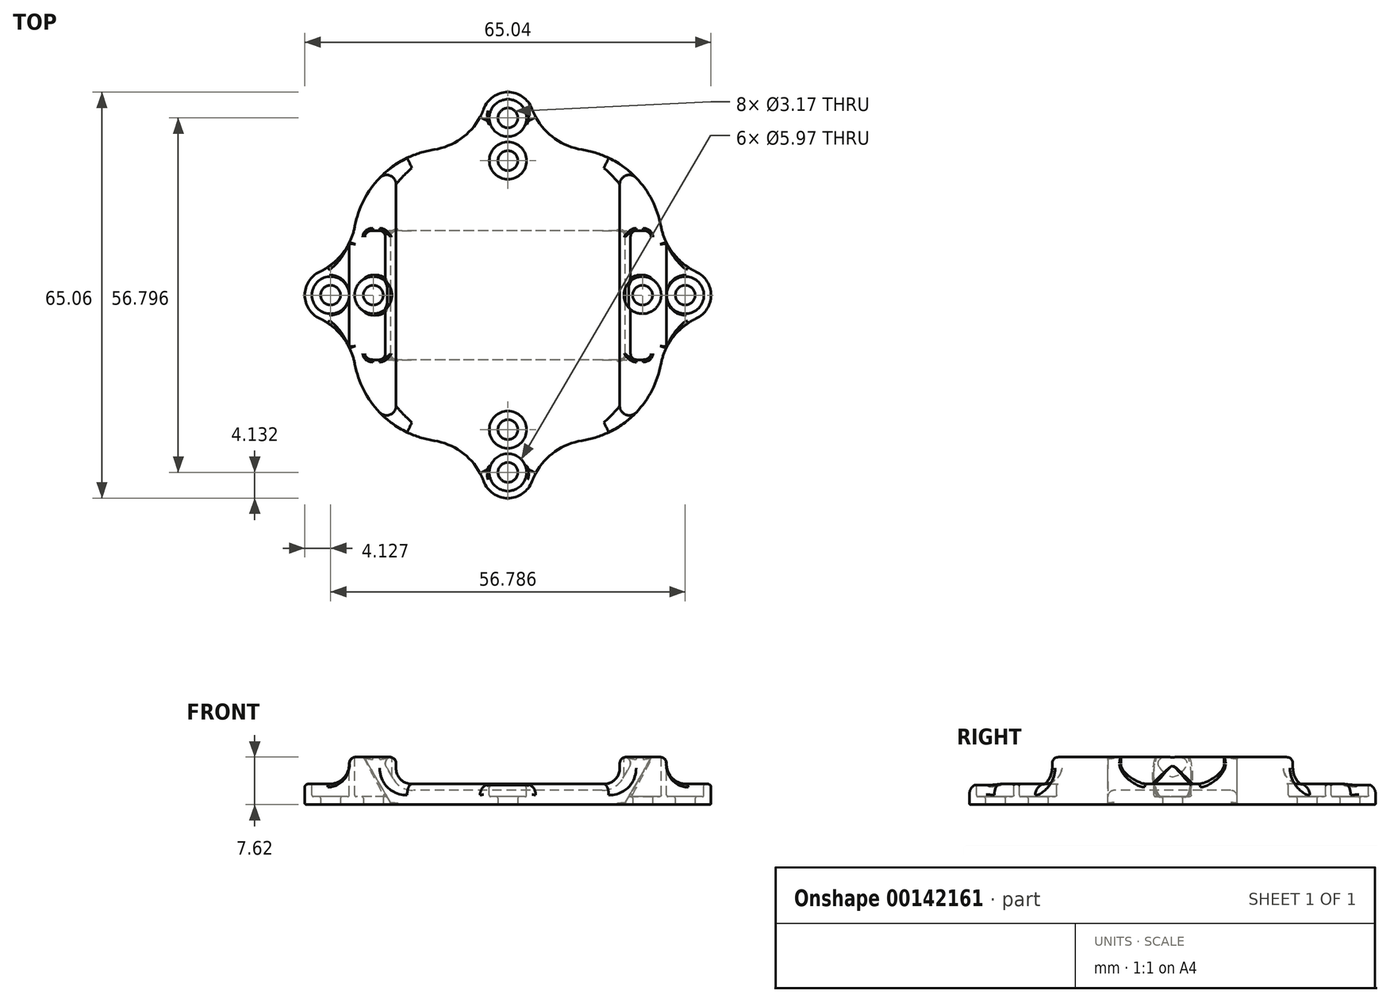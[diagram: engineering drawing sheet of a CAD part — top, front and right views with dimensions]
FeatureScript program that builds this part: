
annotation { "Feature Type Name" : "Feature", "Feature Type Description" : "" }
export const myFeature = defineFeature(function(context is Context, id is Id, definition is map)
    precondition{}
    {
        {
            var Q0;
            Q0=qCreatedBy(makeId("Top.planeOp"),FACE);
            var sketch = newSketch(context, id + "F0", { "sketchPlane" : qUnion([Q0])});
            skLineSegment(sketch, "E0", {"start": v(-21.55, 0) * mm, "end": v(0, 21.55) * mm});
            skLineSegment(sketch, "E1", {"start": v(0, 21.55) * mm, "end": v(21.55, 0) * mm});
            skLineSegment(sketch, "E2", {"start": v(21.55, 0) * mm, "end": v(0, -21.55) * mm});
            skLineSegment(sketch, "E3", {"start": v(0, -21.55) * mm, "end": v(-21.55, 0) * mm});
            skCircle(sketch, "E4", {"center": v(0, 21.55) * mm, "radius": 1.59 * mm});
            skCircle(sketch, "E5", {"center": v(-21.55, 0) * mm, "radius": 1.59 * mm});
            skCircle(sketch, "E6", {"center": v(0, -21.55) * mm, "radius": 1.59 * mm});
            skCircle(sketch, "E7", {"center": v(21.55, 0) * mm, "radius": 1.59 * mm});
            skCircle(sketch, "E8", {"center": v(0, 28.4) * mm, "radius": 1.59 * mm});
            skCircle(sketch, "E9", {"center": v(0, -28.4) * mm, "radius": 1.59 * mm});
            skCircle(sketch, "E10", {"center": v(28.4, 0) * mm, "radius": 1.59 * mm});
            skCircle(sketch, "E11", {"center": v(-28.4, 0) * mm, "radius": 1.59 * mm});
            skLineSegment(sketch, "E12.bottom", {"start": v(9.53, 23.5) * mm, "end": v(-9.53, 23.5) * mm});
            skLineSegment(sketch, "E12.top", {"start": v(9.53, -23.5) * mm, "end": v(-9.53, -23.5) * mm});
            skLineSegment(sketch, "E12.left", {"start": v(24.77, 8.26) * mm, "end": v(24.77, -8.26) * mm});
            skLineSegment(sketch, "E12.right", {"start": v(-24.77, 8.26) * mm, "end": v(-24.77, -8.26) * mm});
            skPoint(sketch, "E12.middle", {"position": v(0, 0) * mm});
            skLineSegment(sketch, "E13.bottom", {"start": v(0, 32.53) * mm, "end": v(0, 32.53) * mm});
            skLineSegment(sketch, "E13.top", {"start": v(4.13, 10.58) * mm, "end": v(-4.13, 10.58) * mm});
            skLineSegment(sketch, "E13.left", {"start": v(4.13, 28.4) * mm, "end": v(4.13, 10.58) * mm});
            skLineSegment(sketch, "E13.right", {"start": v(-4.13, 28.4) * mm, "end": v(-4.13, 10.58) * mm});
            skLineSegment(sketch, "E14.bottom", {"start": v(28.4, 4.13) * mm, "end": v(10.58, 4.13) * mm});
            skLineSegment(sketch, "E14.top", {"start": v(28.4, -4.13) * mm, "end": v(10.58, -4.13) * mm});
            skLineSegment(sketch, "E14.left", {"start": v(32.52, 0) * mm, "end": v(32.52, 0) * mm});
            skLineSegment(sketch, "E14.right", {"start": v(10.58, 4.13) * mm, "end": v(10.58, -4.13) * mm});
            skLineSegment(sketch, "E15.bottom", {"start": v(4.13, -10.58) * mm, "end": v(-4.13, -10.58) * mm});
            skLineSegment(sketch, "E15.top", {"start": v(0, -32.53) * mm, "end": v(0, -32.53) * mm});
            skLineSegment(sketch, "E15.left", {"start": v(4.13, -10.58) * mm, "end": v(4.13, -28.4) * mm});
            skLineSegment(sketch, "E15.right", {"start": v(-4.13, -10.58) * mm, "end": v(-4.13, -28.4) * mm});
            skLineSegment(sketch, "E16.bottom", {"start": v(-10.58, 4.13) * mm, "end": v(-28.4, 4.13) * mm});
            skLineSegment(sketch, "E16.top", {"start": v(-10.58, -4.13) * mm, "end": v(-28.4, -4.13) * mm});
            skLineSegment(sketch, "E16.left", {"start": v(-10.58, 4.13) * mm, "end": v(-10.58, -4.13) * mm});
            skLineSegment(sketch, "E16.right", {"start": v(-32.52, 0) * mm, "end": v(-32.52, 0) * mm});
            skPoint(sketch, "E17.visualSharp", {"position": v(-32.52, 4.13) * mm});
            skArc(sketch, "E17.filletArc", {"start": v(-28.4, 4.13) * mm, "mid": v(-31.31, 2.92) * mm, "end": v(-32.52, 0) * mm});
            skPoint(sketch, "E18.visualSharp", {"position": v(-32.52, -4.13) * mm});
            skArc(sketch, "E18.filletArc", {"start": v(-32.52, 0) * mm, "mid": v(-31.31, -2.92) * mm, "end": v(-28.4, -4.13) * mm});
            skPoint(sketch, "E19.visualSharp", {"position": v(32.52, 4.13) * mm});
            skArc(sketch, "E19.filletArc", {"start": v(32.52, 0) * mm, "mid": v(31.31, 2.92) * mm, "end": v(28.4, 4.13) * mm});
            skPoint(sketch, "E20.visualSharp", {"position": v(32.52, -4.13) * mm});
            skArc(sketch, "E20.filletArc", {"start": v(28.4, -4.13) * mm, "mid": v(31.31, -2.92) * mm, "end": v(32.52, 0) * mm});
            skPoint(sketch, "E21.visualSharp", {"position": v(4.13, -32.53) * mm});
            skArc(sketch, "E21.filletArc", {"start": v(0, -32.53) * mm, "mid": v(2.92, -31.32) * mm, "end": v(4.13, -28.4) * mm});
            skPoint(sketch, "E22.visualSharp", {"position": v(-4.13, -32.53) * mm});
            skArc(sketch, "E22.filletArc", {"start": v(-4.13, -28.4) * mm, "mid": v(-2.92, -31.32) * mm, "end": v(0, -32.53) * mm});
            skPoint(sketch, "E23.visualSharp", {"position": v(-4.13, 32.53) * mm});
            skArc(sketch, "E23.filletArc", {"start": v(0, 32.53) * mm, "mid": v(-2.92, 31.32) * mm, "end": v(-4.13, 28.4) * mm});
            skPoint(sketch, "E24.visualSharp", {"position": v(4.13, 32.53) * mm});
            skArc(sketch, "E24.filletArc", {"start": v(4.13, 28.4) * mm, "mid": v(2.92, 31.32) * mm, "end": v(0, 32.53) * mm});
            skPoint(sketch, "E25.visualSharp", {"position": v(-24.77, 23.5) * mm});
            skArc(sketch, "E25.filletArc", {"start": v(-9.53, 23.5) * mm, "mid": v(-20.3, 19.03) * mm, "end": v(-24.77, 8.26) * mm});
            skPoint(sketch, "E26.visualSharp", {"position": v(24.77, 23.5) * mm});
            skArc(sketch, "E26.filletArc", {"start": v(24.77, 8.26) * mm, "mid": v(20.3, 19.03) * mm, "end": v(9.53, 23.5) * mm});
            skPoint(sketch, "E27.visualSharp", {"position": v(24.77, -23.5) * mm});
            skArc(sketch, "E27.filletArc", {"start": v(9.53, -23.5) * mm, "mid": v(20.3, -19.03) * mm, "end": v(24.77, -8.26) * mm});
            skPoint(sketch, "E28.visualSharp", {"position": v(-24.77, -23.5) * mm});
            skArc(sketch, "E28.filletArc", {"start": v(-24.77, -8.26) * mm, "mid": v(-20.3, -19.03) * mm, "end": v(-9.53, -23.5) * mm});
            skSolve(sketch);
        }
        {
            var Q0;
            Q0=makeQuery(id+"F0.imprint","IMPRINT",FACE,{"disambiguationData":[TD([[makeQuery(id+"F0.imprint","IMPRINT",EDGE,{"derivedFrom":sQuery(id+"F0.wireOp",EDGE,"E8")}),-1.0]])]});
            var Q1;
            Q1=makeQuery(id+"F0.imprint","IMPRINT",FACE,{"disambiguationData":[TD([[makeQuery(id+"F0.imprint","IMPRINT",EDGE,{"derivedFrom":sQuery(id+"F0.wireOp",EDGE,"E9")}),-1.0]])]});
            var Q2;
            Q2=makeQuery(id+"F0.imprint","IMPRINT",FACE,{"disambiguationData":[TD([[makeQuery(id+"F0.imprint","IMPRINT",EDGE,{"derivedFrom":sQuery(id+"F0.wireOp",EDGE,"E10")}),-1.0]])]});
            var Q3;
            Q3=makeQuery(id+"F0.imprint","IMPRINT",FACE,{"disambiguationData":[TD([[makeQuery(id+"F0.imprint","IMPRINT",EDGE,{"derivedFrom":sQuery(id+"F0.wireOp",EDGE,"E11")}),-1.0]])]});
            var Q4;
            {var subQ0=sQuery(id+"F0.wireOp",EDGE,"E25.filletArc");Q4=makeQuery(id+"F0.imprint","IMPRINT",FACE,{"disambiguationData":[TD([[makeQuery(id+"F0.imprint","IMPRINT",EDGE,{"derivedFrom":subQ0}),1.0]])]});}
            var Q5;
            {var subQ5=sQuery(id+"F0.wireOp",EDGE,"E26.filletArc");Q5=makeQuery(id+"F0.imprint","IMPRINT",FACE,{"disambiguationData":[TD([[makeQuery(id+"F0.imprint","IMPRINT",EDGE,{"derivedFrom":subQ5}),1.0]])]});}
            var Q6;
            {var subQ5=sQuery(id+"F0.wireOp",EDGE,"E27.filletArc");Q6=makeQuery(id+"F0.imprint","IMPRINT",FACE,{"disambiguationData":[TD([[makeQuery(id+"F0.imprint","IMPRINT",EDGE,{"derivedFrom":subQ5}),1.0]])]});}
            var Q7;
            {var subQ5=sQuery(id+"F0.wireOp",EDGE,"E28.filletArc");Q7=makeQuery(id+"F0.imprint","IMPRINT",FACE,{"disambiguationData":[TD([[makeQuery(id+"F0.imprint","IMPRINT",EDGE,{"derivedFrom":subQ5}),1.0]])]});}
            var Q8;
            {var subQ5=sQuery(id+"F0.wireOp",EDGE,"E0");var subQ7=sQuery(id+"F0.wireOp",EDGE,"E5");var subQ8=makeQuery(id+"F0.imprint","INTERSECT",VERTEX,{"derivedFrom":[subQ5,subQ7]});Q8=makeQuery(id+"F0.imprint","IMPRINT",FACE,{"disambiguationData":[TD([[makeQuery(id+"F0.imprint","IMPRINT",EDGE,{"disambiguationData":[TD([[subQ8,-1.0]])],"derivedFrom":subQ5}),1.0]])]});}
            var Q9;
            {var subQ1=sQuery(id+"F0.wireOp",EDGE,"E0");var subQ9=sQuery(id+"F0.wireOp",EDGE,"E13.right");var subQ11=makeQuery(id+"F0.imprint","INTERSECT",VERTEX,{"derivedFrom":[subQ1,subQ9]});Q9=makeQuery(id+"F0.imprint","IMPRINT",FACE,{"disambiguationData":[TD([[makeQuery(id+"F0.imprint","IMPRINT",EDGE,{"disambiguationData":[TD([[subQ11,-1.0]])],"derivedFrom":subQ1}),1.0]])]});}
            var Q10;
            {var subQ0=sQuery(id+"F0.wireOp",EDGE,"E14.bottom");var subQ6=sQuery(id+"F0.wireOp",EDGE,"E1");var subQ11=makeQuery(id+"F0.imprint","INTERSECT",VERTEX,{"derivedFrom":[subQ6,subQ0]});Q10=makeQuery(id+"F0.imprint","IMPRINT",FACE,{"disambiguationData":[TD([[makeQuery(id+"F0.imprint","IMPRINT",EDGE,{"disambiguationData":[TD([[subQ11,-1.0]])],"derivedFrom":subQ6}),1.0]])]});}
            var Q11;
            {var subQ0=sQuery(id+"F0.wireOp",EDGE,"E15.left");var subQ9=sQuery(id+"F0.wireOp",EDGE,"E2");var subQ11=makeQuery(id+"F0.imprint","INTERSECT",VERTEX,{"derivedFrom":[subQ9,subQ0]});Q11=makeQuery(id+"F0.imprint","IMPRINT",FACE,{"disambiguationData":[TD([[makeQuery(id+"F0.imprint","IMPRINT",EDGE,{"disambiguationData":[TD([[subQ11,-1.0]])],"derivedFrom":subQ9}),1.0]])]});}
            var Q12;
            {var subQ10=sQuery(id+"F0.wireOp",EDGE,"E13.top");Q12=makeQuery(id+"F0.imprint","IMPRINT",FACE,{"disambiguationData":[TD([[makeQuery(id+"F0.imprint","IMPRINT",EDGE,{"derivedFrom":subQ10}),1.0]])]});}
            var Q13;
            {var subQ0=sQuery(id+"F0.wireOp",EDGE,"E13.top");Q13=makeQuery(id+"F0.imprint","IMPRINT",FACE,{"disambiguationData":[TD([[makeQuery(id+"F0.imprint","IMPRINT",EDGE,{"derivedFrom":subQ0}),-1.0]])]});}
            var Q14;
            {var subQ0=sQuery(id+"F0.wireOp",EDGE,"E16.left");Q14=makeQuery(id+"F0.imprint","IMPRINT",FACE,{"disambiguationData":[TD([[makeQuery(id+"F0.imprint","IMPRINT",EDGE,{"derivedFrom":subQ0}),-1.0]])]});}
            var Q15;
            {var subQ8=sQuery(id+"F0.wireOp",EDGE,"E15.bottom");Q15=makeQuery(id+"F0.imprint","IMPRINT",FACE,{"disambiguationData":[TD([[makeQuery(id+"F0.imprint","IMPRINT",EDGE,{"derivedFrom":subQ8}),1.0]])]});}
            var Q16;
            {var subQ0=sQuery(id+"F0.wireOp",EDGE,"E14.right");Q16=makeQuery(id+"F0.imprint","IMPRINT",FACE,{"disambiguationData":[TD([[makeQuery(id+"F0.imprint","IMPRINT",EDGE,{"derivedFrom":subQ0}),1.0]])]});}
            var Q17;
            {var subQ0=sQuery(id+"F0.wireOp",EDGE,"E16.left");Q17=makeQuery(id+"F0.imprint","IMPRINT",FACE,{"disambiguationData":[TD([[makeQuery(id+"F0.imprint","IMPRINT",EDGE,{"derivedFrom":subQ0}),-1.0]])]});}
            extrude(context, id + "F1", {"entities" : qUnion([Q0, Q1, Q2, Q3, Q4, Q5, Q6, Q7, Q8, Q9, Q10, Q11, Q12, Q13, Q14, Q15, Q16, Q17]), "depth" : 7.62 * mm});
        }
        {
            var Q0;
            Q0=makeQuery(id+"F1.opExtrude","SWEPT_EDGE",EDGE,{"disambiguationData":[OSD([sQuery(id+"F0.wireOp",EDGE,"E12.bottom"),sQuery(id+"F0.wireOp",EDGE,"E13.left")])]});
            var Q1;
            Q1=makeQuery(id+"F1.opExtrude","SWEPT_EDGE",EDGE,{"disambiguationData":[OSD([sQuery(id+"F0.wireOp",EDGE,"E12.bottom"),sQuery(id+"F0.wireOp",EDGE,"E13.right")])]});
            var Q2;
            Q2=makeQuery(id+"F1.opExtrude","SWEPT_EDGE",EDGE,{"disambiguationData":[OSD([sQuery(id+"F0.wireOp",EDGE,"E12.top"),sQuery(id+"F0.wireOp",EDGE,"E15.right")])]});
            var Q3;
            Q3=makeQuery(id+"F1.opExtrude","SWEPT_EDGE",EDGE,{"disambiguationData":[OSD([sQuery(id+"F0.wireOp",EDGE,"E12.top"),sQuery(id+"F0.wireOp",EDGE,"E15.left")])]});
            fillet(context, id + "F2", {"entities" : qUnion([Q0, Q1, Q2, Q3]), "radius" : 10.16 * mm, "tangentPropagation" : true, "allowEdgeOverflow" : false});
        }
        {
            var Q0;
            Q0=makeQuery(id+"F1.opExtrude","CAP_FACE",FACE,{"disambiguationData":[OSD([sQuery(id+"F0.wireOp",EDGE,"E4"),sQuery(id+"F0.wireOp",EDGE,"E5"),sQuery(id+"F0.wireOp",EDGE,"E6"),sQuery(id+"F0.wireOp",EDGE,"E7"),sQuery(id+"F0.wireOp",EDGE,"E8"),sQuery(id+"F0.wireOp",EDGE,"E9"),sQuery(id+"F0.wireOp",EDGE,"E10"),sQuery(id+"F0.wireOp",EDGE,"E11"),sQuery(id+"F0.wireOp",EDGE,"E12.bottom"),sQuery(id+"F0.wireOp",EDGE,"E12.top"),sQuery(id+"F0.wireOp",EDGE,"E12.left"),sQuery(id+"F0.wireOp",EDGE,"E12.right"),sQuery(id+"F0.wireOp",EDGE,"E13.left"),sQuery(id+"F0.wireOp",EDGE,"E13.right"),sQuery(id+"F0.wireOp",EDGE,"E14.bottom"),sQuery(id+"F0.wireOp",EDGE,"E14.top"),sQuery(id+"F0.wireOp",EDGE,"E15.left"),sQuery(id+"F0.wireOp",EDGE,"E15.right"),sQuery(id+"F0.wireOp",EDGE,"E16.bottom"),sQuery(id+"F0.wireOp",EDGE,"E16.top"),sQuery(id+"F0.wireOp",EDGE,"E17.filletArc"),sQuery(id+"F0.wireOp",EDGE,"E18.filletArc"),sQuery(id+"F0.wireOp",EDGE,"E19.filletArc"),sQuery(id+"F0.wireOp",EDGE,"E20.filletArc"),sQuery(id+"F0.wireOp",EDGE,"E21.filletArc"),sQuery(id+"F0.wireOp",EDGE,"E22.filletArc"),sQuery(id+"F0.wireOp",EDGE,"E23.filletArc"),sQuery(id+"F0.wireOp",EDGE,"E24.filletArc"),sQuery(id+"F0.wireOp",EDGE,"E25.filletArc"),sQuery(id+"F0.wireOp",EDGE,"E26.filletArc"),sQuery(id+"F0.wireOp",EDGE,"E27.filletArc"),sQuery(id+"F0.wireOp",EDGE,"E28.filletArc")])],"isStart":false});
            var sketch = newSketch(context, id + "F3", { "sketchPlane" : qUnion([Q0])});
            skCircle(sketch, "E29", {"center": v(0, 28.4) * mm, "radius": 2.98 * mm});
            skCircle(sketch, "E30", {"center": v(0, 21.55) * mm, "radius": 2.98 * mm});
            skCircle(sketch, "E31", {"center": v(0, -21.55) * mm, "radius": 2.98 * mm});
            skCircle(sketch, "E32", {"center": v(0, -28.4) * mm, "radius": 2.98 * mm});
            skCircle(sketch, "E33", {"center": v(-21.55, 0) * mm, "radius": 2.98 * mm});
            skCircle(sketch, "E34", {"center": v(21.55, 0) * mm, "radius": 2.98 * mm});
            skCircle(sketch, "E35", {"center": v(28.4, 0) * mm, "radius": 2.98 * mm});
            skCircle(sketch, "E36", {"center": v(-28.4, 0) * mm, "radius": 2.98 * mm});
            skSolve(sketch);
        }
        {
            var Q0;
            Q0 = qSketchRegion(id + "F3", true);
            extrude(context, id + "F4", {"entities" : qUnion([Q0]), "operationType" : NewBodyOperationType.REMOVE, "oppositeDirection" : true, "depth" : 6.35 * mm});
        }
        {
            var Q0;
            Q0=qCreatedBy(makeId("Front.planeOp"),FACE);
            var sketch = newSketch(context, id + "F5", { "sketchPlane" : qUnion([Q0])});
            skLineSegment(sketch, "E37.bottom", {"start": v(17.9, 3.3) * mm, "end": v(-17.9, 3.3) * mm});
            skLineSegment(sketch, "E37.top", {"start": v(17.9, 28.7) * mm, "end": v(-17.9, 28.7) * mm});
            skLineSegment(sketch, "E37.left", {"start": v(17.9, 3.3) * mm, "end": v(17.9, 28.7) * mm});
            skLineSegment(sketch, "E37.right", {"start": v(-17.9, 3.3) * mm, "end": v(-17.9, 28.7) * mm});
            skPoint(sketch, "E37.middle", {"position": v(0, 16) * mm});
            skPoint(sketch, "E38.visualSharp", {"position": v(-17.9, 3.3) * mm});
            skLineSegment(sketch, "E38.filletArc", {"start": v(-17.9, 3.3) * mm, "end": v(-17.9, 3.3) * mm});
            skPoint(sketch, "E39.visualSharp", {"position": v(17.9, 3.3) * mm});
            skLineSegment(sketch, "E39.filletArc", {"start": v(17.9, 3.3) * mm, "end": v(17.9, 3.3) * mm});
            skLineSegment(sketch, "E40.bottom", {"start": v(28.58, 3.3) * mm, "end": v(38.1, 3.3) * mm});
            skLineSegment(sketch, "E40.top", {"start": v(25.4, 28.7) * mm, "end": v(38.1, 28.7) * mm});
            skLineSegment(sketch, "E40.left", {"start": v(25.4, 6.48) * mm, "end": v(25.4, 28.7) * mm});
            skLineSegment(sketch, "E40.right", {"start": v(38.1, 3.3) * mm, "end": v(38.1, 28.7) * mm});
            skLineSegment(sketch, "E41.bottom", {"start": v(-28.58, 3.3) * mm, "end": v(-38.1, 3.3) * mm});
            skLineSegment(sketch, "E41.top", {"start": v(-25.4, 28.7) * mm, "end": v(-38.1, 28.7) * mm});
            skLineSegment(sketch, "E41.left", {"start": v(-25.4, 6.48) * mm, "end": v(-25.4, 28.7) * mm});
            skLineSegment(sketch, "E41.right", {"start": v(-38.1, 3.3) * mm, "end": v(-38.1, 28.7) * mm});
            skPoint(sketch, "E42.visualSharp", {"position": v(-25.4, 3.3) * mm});
            skArc(sketch, "E42.filletArc", {"start": v(-28.58, 3.3) * mm, "mid": v(-26.33, 4.23) * mm, "end": v(-25.4, 6.48) * mm});
            skPoint(sketch, "E43.visualSharp", {"position": v(25.4, 3.3) * mm});
            skArc(sketch, "E43.filletArc", {"start": v(25.4, 6.48) * mm, "mid": v(26.33, 4.23) * mm, "end": v(28.58, 3.3) * mm});
            skSolve(sketch);
        }
        {
            var Q0;
            Q0 = qSketchRegion(id + "F5", true);
            extrude(context, id + "F6", {"entities" : qUnion([Q0]), "operationType" : NewBodyOperationType.REMOVE, "endBound" : BoundingType.SYMMETRIC, "oppositeDirection" : true, "depth" : 152.4 * mm});
        }
        {
            var Q0;
            Q0=qCreatedBy(makeId("Right.planeOp"),FACE);
            var sketch = newSketch(context, id + "F7", { "sketchPlane" : qUnion([Q0])});
            skLineSegment(sketch, "E44.bottom", {"start": v(-10.35, 0) * mm, "end": v(10.35, 0) * mm});
            skLineSegment(sketch, "E44.top", {"start": v(-10.35, 2.29) * mm, "end": v(10.35, 2.29) * mm});
            skLineSegment(sketch, "E44.left", {"start": v(-10.35, 0) * mm, "end": v(-10.35, 2.29) * mm});
            skLineSegment(sketch, "E44.right", {"start": v(10.35, 0) * mm, "end": v(10.35, 2.29) * mm});
            skPoint(sketch, "E44.middle", {"position": v(0, 1.14) * mm});
            skSolve(sketch);
        }
        {
            var Q0;
            Q0 = qSketchRegion(id + "F7", true);
            extrude(context, id + "F8", {"entities" : qUnion([Q0]), "operationType" : NewBodyOperationType.REMOVE, "endBound" : BoundingType.SYMMETRIC, "depth" : 35.56 * mm});
        }
        {
            var Q0;
            Q0=qCreatedBy(makeId("Front.planeOp"),FACE);
            var sketch = newSketch(context, id + "F9", { "sketchPlane" : qUnion([Q0])});
            skLineSegment(sketch, "E45", {"start": v(-55.42, 2.54) * mm, "end": v(-11.43, 27.94) * mm});
            skLineSegment(sketch, "E46", {"start": v(11.43, 27.94) * mm, "end": v(55.42, 2.54) * mm});
            skSolve(sketch);
        }
        {
            var Q0;
            Q0=makeQuery(id+"F6.boolean.opBoolean","INTERSECT",EDGE,{"derivedFrom":[makeQuery(id+"F1.opExtrude","SWEPT_FACE",FACE,{"disambiguationData":[OSD([sQuery(id+"F0.wireOp",EDGE,"E28.filletArc")])]}),makeQuery(id+"F6.opExtrude","SWEPT_FACE",FACE,{"disambiguationData":[OSD([sQuery(id+"F5.wireOp",EDGE,"E37.right")])]})]});
            var Q1;
            Q1=makeQuery(id+"F6.boolean.opBoolean","INTERSECT",EDGE,{"derivedFrom":[makeQuery(id+"F1.opExtrude","SWEPT_FACE",FACE,{"disambiguationData":[OSD([sQuery(id+"F0.wireOp",EDGE,"E27.filletArc")])]}),makeQuery(id+"F6.opExtrude","SWEPT_FACE",FACE,{"disambiguationData":[OSD([sQuery(id+"F5.wireOp",EDGE,"E37.left")])]})]});
            var Q2;
            Q2=makeQuery(id+"F6.boolean.opBoolean","INTERSECT",EDGE,{"derivedFrom":[makeQuery(id+"F1.opExtrude","SWEPT_FACE",FACE,{"disambiguationData":[OSD([sQuery(id+"F0.wireOp",EDGE,"E25.filletArc")])]}),makeQuery(id+"F6.opExtrude","SWEPT_FACE",FACE,{"disambiguationData":[OSD([sQuery(id+"F5.wireOp",EDGE,"E37.right")])]})]});
            var Q3;
            Q3=makeQuery(id+"F6.boolean.opBoolean","INTERSECT",EDGE,{"derivedFrom":[makeQuery(id+"F1.opExtrude","SWEPT_FACE",FACE,{"disambiguationData":[OSD([sQuery(id+"F0.wireOp",EDGE,"E26.filletArc")])]}),makeQuery(id+"F6.opExtrude","SWEPT_FACE",FACE,{"disambiguationData":[OSD([sQuery(id+"F5.wireOp",EDGE,"E37.left")])]})]});
            fillet(context, id + "F10", {"entities" : qUnion([Q0, Q1, Q2, Q3]), "radius" : 1.52 * mm, "allowEdgeOverflow" : false});
        }
        {
            var Q0;
            Q0=makeQuery(id+"F6.boolean.opBoolean","COPY",EDGE,{"derivedFrom":makeQuery(id+"F6.opExtrude","SWEPT_EDGE",EDGE,{"disambiguationData":[OSD([sQuery(id+"F5.wireOp",EDGE,"E37.bottom"),sQuery(id+"F5.wireOp",EDGE,"E37.right")])]})});
            var Q1;
            Q1=makeQuery(id+"F6.boolean.opBoolean","COPY",EDGE,{"derivedFrom":makeQuery(id+"F6.opExtrude","SWEPT_EDGE",EDGE,{"disambiguationData":[OSD([sQuery(id+"F5.wireOp",EDGE,"E37.bottom"),sQuery(id+"F5.wireOp",EDGE,"E37.left")])]})});
            fillet(context, id + "F11", {"entities" : qUnion([Q0, Q1]), "radius" : 2.54 * mm, "tangentPropagation" : true, "allowEdgeOverflow" : false});
        }
        {
            var Q0;
            Q0=qCreatedBy(makeId("Right.planeOp"),FACE);
            var Q1;
            Q1=sQuery(id+"F9.wireOp",EDGE,"E45");
            cPlane(context, id + "F12", {"entities" : qUnion([Q0, Q1]), "cplaneType" : CPlaneType.LINE_ANGLE, "offset" : 25.4 * mm, "angle" : 0 * degree, "width" : 152.4 * mm, "height" : 152.4 * mm});
        }
        {
            var Q0;
            Q0=qCreatedBy(id+"F12.planeOp",FACE);
            var sketch = newSketch(context, id + "F13", { "sketchPlane" : qUnion([Q0])});
            skLineSegment(sketch, "E47.bottom", {"start": v(-13.84, -10.35) * mm, "end": v(-16.12, -10.35) * mm});
            skLineSegment(sketch, "E47.top", {"start": v(-13.84, 10.35) * mm, "end": v(-16.12, 10.35) * mm});
            skLineSegment(sketch, "E47.left", {"start": v(-13.84, -10.35) * mm, "end": v(-13.84, 10.35) * mm});
            skLineSegment(sketch, "E47.right", {"start": v(-16.12, -10.35) * mm, "end": v(-16.12, 10.35) * mm});
            skPoint(sketch, "E47.middle", {"position": v(-14.98, 0) * mm});
            skSolve(sketch);
        }
        {
            var Q0;
            Q0 = qSketchRegion(id + "F13", true);
            extrude(context, id + "F14", {"entities" : qUnion([Q0]), "operationType" : NewBodyOperationType.REMOVE, "oppositeDirection" : true, "depth" : 25.4 * mm});
        }
        {
            var Q0;
            Q0=qCreatedBy(makeId("Right.planeOp"),FACE);
            var Q1;
            Q1=sQuery(id+"F9.wireOp",EDGE,"E46");
            cPlane(context, id + "F15", {"entities" : qUnion([Q0, Q1]), "cplaneType" : CPlaneType.LINE_ANGLE, "offset" : 25.4 * mm, "angle" : 0 * degree, "width" : 152.4 * mm, "height" : 152.4 * mm});
        }
        {
            var Q0;
            Q0=qCreatedBy(id+"F15.planeOp",FACE);
            var sketch = newSketch(context, id + "F16", { "sketchPlane" : qUnion([Q0])});
            skLineSegment(sketch, "E48.bottom", {"start": v(13.84, -10.35) * mm, "end": v(16.12, -10.35) * mm});
            skLineSegment(sketch, "E48.top", {"start": v(13.84, 10.35) * mm, "end": v(16.12, 10.35) * mm});
            skLineSegment(sketch, "E48.left", {"start": v(13.84, -10.35) * mm, "end": v(13.84, 10.35) * mm});
            skLineSegment(sketch, "E48.right", {"start": v(16.12, -10.35) * mm, "end": v(16.12, 10.35) * mm});
            skPoint(sketch, "E48.middle", {"position": v(14.98, 0) * mm});
            skSolve(sketch);
        }
        {
            var Q0;
            Q0 = qSketchRegion(id + "F16", true);
            extrude(context, id + "F17", {"entities" : qUnion([Q0]), "operationType" : NewBodyOperationType.REMOVE, "depth" : 25.4 * mm});
        }
        {
            var Q0;
            Q0=makeQuery(id+"F17.boolean.opBoolean","INTERSECT",EDGE,{"derivedFrom":[makeQuery(id+"F8.boolean.opBoolean","COPY",FACE,{"derivedFrom":makeQuery(id+"F8.opExtrude","SWEPT_FACE",FACE,{"disambiguationData":[OSD([sQuery(id+"F7.wireOp",EDGE,"E44.top")])]})}),makeQuery(id+"F17.opExtrude","SWEPT_FACE",FACE,{"disambiguationData":[OSD([sQuery(id+"F16.wireOp",EDGE,"E48.left")])]})]});
            var Q1;
            Q1=makeQuery(id+"F14.boolean.opBoolean","INTERSECT",EDGE,{"derivedFrom":[makeQuery(id+"F8.boolean.opBoolean","COPY",FACE,{"derivedFrom":makeQuery(id+"F8.opExtrude","SWEPT_FACE",FACE,{"disambiguationData":[OSD([sQuery(id+"F7.wireOp",EDGE,"E44.top")])]})}),makeQuery(id+"F14.opExtrude","SWEPT_FACE",FACE,{"disambiguationData":[OSD([sQuery(id+"F13.wireOp",EDGE,"E47.left")])]})]});
            fillet(context, id + "F18", {"entities" : qUnion([Q0, Q1]), "radius" : 3.8 * mm, "tangentPropagation" : true, "allowEdgeOverflow" : false});
        }
        {
            var Q0;
            {var subQ0=sQuery(id+"F0.wireOp",EDGE,"E14.top");var subQ1=sQuery(id+"F0.wireOp",EDGE,"E12.left");var subQ2=sQuery(id+"F0.wireOp",EDGE,"E14.bottom");var subQ3=sQuery(id+"F0.wireOp",EDGE,"E27.filletArc");var subQ4=sQuery(id+"F0.wireOp",EDGE,"E26.filletArc");Q0=makeQuery(id+"F17.boolean.opBoolean","INTERSECT",EDGE,{"disambiguationData":[OD(0.0)],"derivedFrom":[makeQuery(id+"F6.boolean.opBoolean","SPLIT",FACE,{"disambiguationData":[TD([makeQuery(id+"F1.opExtrude","SWEPT_FACE",FACE,{"disambiguationData":[OSD([subQ4])]})])],"derivedFrom":makeQuery(id+"F1.opExtrude","CAP_FACE",FACE,{"disambiguationData":[OSD([sQuery(id+"F0.wireOp",EDGE,"E4"),sQuery(id+"F0.wireOp",EDGE,"E5"),sQuery(id+"F0.wireOp",EDGE,"E6"),sQuery(id+"F0.wireOp",EDGE,"E7"),sQuery(id+"F0.wireOp",EDGE,"E8"),sQuery(id+"F0.wireOp",EDGE,"E9"),sQuery(id+"F0.wireOp",EDGE,"E10"),sQuery(id+"F0.wireOp",EDGE,"E11"),sQuery(id+"F0.wireOp",EDGE,"E12.bottom"),sQuery(id+"F0.wireOp",EDGE,"E12.top"),subQ1,sQuery(id+"F0.wireOp",EDGE,"E12.right"),sQuery(id+"F0.wireOp",EDGE,"E13.left"),sQuery(id+"F0.wireOp",EDGE,"E13.right"),subQ2,subQ0,sQuery(id+"F0.wireOp",EDGE,"E15.left"),sQuery(id+"F0.wireOp",EDGE,"E15.right"),sQuery(id+"F0.wireOp",EDGE,"E16.bottom"),sQuery(id+"F0.wireOp",EDGE,"E16.top"),sQuery(id+"F0.wireOp",EDGE,"E17.filletArc"),sQuery(id+"F0.wireOp",EDGE,"E18.filletArc"),sQuery(id+"F0.wireOp",EDGE,"E19.filletArc"),sQuery(id+"F0.wireOp",EDGE,"E20.filletArc"),sQuery(id+"F0.wireOp",EDGE,"E21.filletArc"),sQuery(id+"F0.wireOp",EDGE,"E22.filletArc"),sQuery(id+"F0.wireOp",EDGE,"E23.filletArc"),sQuery(id+"F0.wireOp",EDGE,"E24.filletArc"),sQuery(id+"F0.wireOp",EDGE,"E25.filletArc"),subQ4,subQ3,sQuery(id+"F0.wireOp",EDGE,"E28.filletArc")])],"isStart":false})}),makeQuery(id+"F17.opExtrude","SWEPT_FACE",FACE,{"disambiguationData":[OSD([sQuery(id+"F16.wireOp",EDGE,"E48.left")])]})]});}
            var Q1;
            {var subQ0=sQuery(id+"F0.wireOp",EDGE,"E14.top");var subQ1=sQuery(id+"F0.wireOp",EDGE,"E12.left");var subQ2=sQuery(id+"F0.wireOp",EDGE,"E14.bottom");var subQ3=sQuery(id+"F0.wireOp",EDGE,"E27.filletArc");var subQ4=sQuery(id+"F0.wireOp",EDGE,"E26.filletArc");Q1=makeQuery(id+"F17.boolean.opBoolean","INTERSECT",EDGE,{"disambiguationData":[OD(1.0)],"derivedFrom":[makeQuery(id+"F6.boolean.opBoolean","SPLIT",FACE,{"disambiguationData":[TD([makeQuery(id+"F1.opExtrude","SWEPT_FACE",FACE,{"disambiguationData":[OSD([subQ4])]})])],"derivedFrom":makeQuery(id+"F1.opExtrude","CAP_FACE",FACE,{"disambiguationData":[OSD([sQuery(id+"F0.wireOp",EDGE,"E4"),sQuery(id+"F0.wireOp",EDGE,"E5"),sQuery(id+"F0.wireOp",EDGE,"E6"),sQuery(id+"F0.wireOp",EDGE,"E7"),sQuery(id+"F0.wireOp",EDGE,"E8"),sQuery(id+"F0.wireOp",EDGE,"E9"),sQuery(id+"F0.wireOp",EDGE,"E10"),sQuery(id+"F0.wireOp",EDGE,"E11"),sQuery(id+"F0.wireOp",EDGE,"E12.bottom"),sQuery(id+"F0.wireOp",EDGE,"E12.top"),subQ1,sQuery(id+"F0.wireOp",EDGE,"E12.right"),sQuery(id+"F0.wireOp",EDGE,"E13.left"),sQuery(id+"F0.wireOp",EDGE,"E13.right"),subQ2,subQ0,sQuery(id+"F0.wireOp",EDGE,"E15.left"),sQuery(id+"F0.wireOp",EDGE,"E15.right"),sQuery(id+"F0.wireOp",EDGE,"E16.bottom"),sQuery(id+"F0.wireOp",EDGE,"E16.top"),sQuery(id+"F0.wireOp",EDGE,"E17.filletArc"),sQuery(id+"F0.wireOp",EDGE,"E18.filletArc"),sQuery(id+"F0.wireOp",EDGE,"E19.filletArc"),sQuery(id+"F0.wireOp",EDGE,"E20.filletArc"),sQuery(id+"F0.wireOp",EDGE,"E21.filletArc"),sQuery(id+"F0.wireOp",EDGE,"E22.filletArc"),sQuery(id+"F0.wireOp",EDGE,"E23.filletArc"),sQuery(id+"F0.wireOp",EDGE,"E24.filletArc"),sQuery(id+"F0.wireOp",EDGE,"E25.filletArc"),subQ4,subQ3,sQuery(id+"F0.wireOp",EDGE,"E28.filletArc")])],"isStart":false})}),makeQuery(id+"F17.opExtrude","SWEPT_FACE",FACE,{"disambiguationData":[OSD([sQuery(id+"F16.wireOp",EDGE,"E48.left")])]})]});}
            var Q2;
            {var subQ0=sQuery(id+"F0.wireOp",EDGE,"E16.top");var subQ1=sQuery(id+"F0.wireOp",EDGE,"E12.right");var subQ2=sQuery(id+"F0.wireOp",EDGE,"E16.bottom");var subQ3=sQuery(id+"F0.wireOp",EDGE,"E28.filletArc");var subQ4=sQuery(id+"F0.wireOp",EDGE,"E25.filletArc");Q2=makeQuery(id+"F14.boolean.opBoolean","INTERSECT",EDGE,{"disambiguationData":[OD(0.0)],"derivedFrom":[makeQuery(id+"F6.boolean.opBoolean","SPLIT",FACE,{"disambiguationData":[TD([makeQuery(id+"F1.opExtrude","SWEPT_FACE",FACE,{"disambiguationData":[OSD([subQ4])]})])],"derivedFrom":makeQuery(id+"F1.opExtrude","CAP_FACE",FACE,{"disambiguationData":[OSD([sQuery(id+"F0.wireOp",EDGE,"E4"),sQuery(id+"F0.wireOp",EDGE,"E5"),sQuery(id+"F0.wireOp",EDGE,"E6"),sQuery(id+"F0.wireOp",EDGE,"E7"),sQuery(id+"F0.wireOp",EDGE,"E8"),sQuery(id+"F0.wireOp",EDGE,"E9"),sQuery(id+"F0.wireOp",EDGE,"E10"),sQuery(id+"F0.wireOp",EDGE,"E11"),sQuery(id+"F0.wireOp",EDGE,"E12.bottom"),sQuery(id+"F0.wireOp",EDGE,"E12.top"),sQuery(id+"F0.wireOp",EDGE,"E12.left"),subQ1,sQuery(id+"F0.wireOp",EDGE,"E13.left"),sQuery(id+"F0.wireOp",EDGE,"E13.right"),sQuery(id+"F0.wireOp",EDGE,"E14.bottom"),sQuery(id+"F0.wireOp",EDGE,"E14.top"),sQuery(id+"F0.wireOp",EDGE,"E15.left"),sQuery(id+"F0.wireOp",EDGE,"E15.right"),subQ2,subQ0,sQuery(id+"F0.wireOp",EDGE,"E17.filletArc"),sQuery(id+"F0.wireOp",EDGE,"E18.filletArc"),sQuery(id+"F0.wireOp",EDGE,"E19.filletArc"),sQuery(id+"F0.wireOp",EDGE,"E20.filletArc"),sQuery(id+"F0.wireOp",EDGE,"E21.filletArc"),sQuery(id+"F0.wireOp",EDGE,"E22.filletArc"),sQuery(id+"F0.wireOp",EDGE,"E23.filletArc"),sQuery(id+"F0.wireOp",EDGE,"E24.filletArc"),subQ4,sQuery(id+"F0.wireOp",EDGE,"E26.filletArc"),sQuery(id+"F0.wireOp",EDGE,"E27.filletArc"),subQ3])],"isStart":false})}),makeQuery(id+"F14.opExtrude","SWEPT_FACE",FACE,{"disambiguationData":[OSD([sQuery(id+"F13.wireOp",EDGE,"E47.left")])]})]});}
            var Q3;
            {var subQ0=sQuery(id+"F0.wireOp",EDGE,"E16.top");var subQ1=sQuery(id+"F0.wireOp",EDGE,"E12.right");var subQ2=sQuery(id+"F0.wireOp",EDGE,"E16.bottom");var subQ3=sQuery(id+"F0.wireOp",EDGE,"E28.filletArc");var subQ4=sQuery(id+"F0.wireOp",EDGE,"E25.filletArc");Q3=makeQuery(id+"F14.boolean.opBoolean","INTERSECT",EDGE,{"disambiguationData":[OD(1.0)],"derivedFrom":[makeQuery(id+"F6.boolean.opBoolean","SPLIT",FACE,{"disambiguationData":[TD([makeQuery(id+"F1.opExtrude","SWEPT_FACE",FACE,{"disambiguationData":[OSD([subQ4])]})])],"derivedFrom":makeQuery(id+"F1.opExtrude","CAP_FACE",FACE,{"disambiguationData":[OSD([sQuery(id+"F0.wireOp",EDGE,"E4"),sQuery(id+"F0.wireOp",EDGE,"E5"),sQuery(id+"F0.wireOp",EDGE,"E6"),sQuery(id+"F0.wireOp",EDGE,"E7"),sQuery(id+"F0.wireOp",EDGE,"E8"),sQuery(id+"F0.wireOp",EDGE,"E9"),sQuery(id+"F0.wireOp",EDGE,"E10"),sQuery(id+"F0.wireOp",EDGE,"E11"),sQuery(id+"F0.wireOp",EDGE,"E12.bottom"),sQuery(id+"F0.wireOp",EDGE,"E12.top"),sQuery(id+"F0.wireOp",EDGE,"E12.left"),subQ1,sQuery(id+"F0.wireOp",EDGE,"E13.left"),sQuery(id+"F0.wireOp",EDGE,"E13.right"),sQuery(id+"F0.wireOp",EDGE,"E14.bottom"),sQuery(id+"F0.wireOp",EDGE,"E14.top"),sQuery(id+"F0.wireOp",EDGE,"E15.left"),sQuery(id+"F0.wireOp",EDGE,"E15.right"),subQ2,subQ0,sQuery(id+"F0.wireOp",EDGE,"E17.filletArc"),sQuery(id+"F0.wireOp",EDGE,"E18.filletArc"),sQuery(id+"F0.wireOp",EDGE,"E19.filletArc"),sQuery(id+"F0.wireOp",EDGE,"E20.filletArc"),sQuery(id+"F0.wireOp",EDGE,"E21.filletArc"),sQuery(id+"F0.wireOp",EDGE,"E22.filletArc"),sQuery(id+"F0.wireOp",EDGE,"E23.filletArc"),sQuery(id+"F0.wireOp",EDGE,"E24.filletArc"),subQ4,sQuery(id+"F0.wireOp",EDGE,"E26.filletArc"),sQuery(id+"F0.wireOp",EDGE,"E27.filletArc"),subQ3])],"isStart":false})}),makeQuery(id+"F14.opExtrude","SWEPT_FACE",FACE,{"disambiguationData":[OSD([sQuery(id+"F13.wireOp",EDGE,"E47.left")])]})]});}
            fillet(context, id + "F19", {"entities" : qUnion([Q0, Q1, Q2, Q3]), "radius" : 1.02 * mm, "allowEdgeOverflow" : false});
        }
        {
            var Q0;
            Q0=makeQuery(id+"F8.boolean.opBoolean","COPY",EDGE,{"derivedFrom":makeQuery(id+"F8.opExtrude","SWEPT_EDGE",EDGE,{"disambiguationData":[OSD([sQuery(id+"F7.wireOp",EDGE,"E44.top"),sQuery(id+"F7.wireOp",EDGE,"E44.right")])]})});
            var Q1;
            Q1=makeQuery(id+"F8.boolean.opBoolean","COPY",EDGE,{"derivedFrom":makeQuery(id+"F8.opExtrude","SWEPT_EDGE",EDGE,{"disambiguationData":[OSD([sQuery(id+"F7.wireOp",EDGE,"E44.top"),sQuery(id+"F7.wireOp",EDGE,"E44.left")])]})});
            var Q2;
            Q2=makeQuery(id+"F17.boolean.opBoolean","COPY",EDGE,{"derivedFrom":makeQuery(id+"F17.opExtrude","SWEPT_EDGE",EDGE,{"disambiguationData":[OSD([sQuery(id+"F16.wireOp",EDGE,"E48.top"),sQuery(id+"F16.wireOp",EDGE,"E48.right")])]})});
            var Q3;
            Q3=makeQuery(id+"F17.boolean.opBoolean","COPY",EDGE,{"derivedFrom":makeQuery(id+"F17.opExtrude","SWEPT_EDGE",EDGE,{"disambiguationData":[OSD([sQuery(id+"F16.wireOp",EDGE,"E48.bottom"),sQuery(id+"F16.wireOp",EDGE,"E48.right")])]})});
            var Q4;
            Q4=makeQuery(id+"F14.boolean.opBoolean","COPY",EDGE,{"derivedFrom":makeQuery(id+"F14.opExtrude","SWEPT_EDGE",EDGE,{"disambiguationData":[OSD([sQuery(id+"F13.wireOp",EDGE,"E47.bottom"),sQuery(id+"F13.wireOp",EDGE,"E47.right")])]})});
            var Q5;
            Q5=makeQuery(id+"F14.boolean.opBoolean","COPY",EDGE,{"derivedFrom":makeQuery(id+"F14.opExtrude","SWEPT_EDGE",EDGE,{"disambiguationData":[OSD([sQuery(id+"F13.wireOp",EDGE,"E47.top"),sQuery(id+"F13.wireOp",EDGE,"E47.right")])]})});
            fillet(context, id + "F20", {"entities" : qUnion([Q0, Q1, Q2, Q3, Q4, Q5]), "radius" : 1.02 * mm, "tangentPropagation" : true, "allowEdgeOverflow" : false});
        }
        {
            var Q0;
            Q0=makeQuery(id+"F1.opExtrude","SWEPT_EDGE",EDGE,{"disambiguationData":[OSD([sQuery(id+"F0.wireOp",EDGE,"E12.left"),sQuery(id+"F0.wireOp",EDGE,"E14.top")])]});
            var Q1;
            Q1=makeQuery(id+"F1.opExtrude","SWEPT_EDGE",EDGE,{"disambiguationData":[OSD([sQuery(id+"F0.wireOp",EDGE,"E12.left"),sQuery(id+"F0.wireOp",EDGE,"E14.bottom")])]});
            var Q2;
            Q2=makeQuery(id+"F1.opExtrude","SWEPT_EDGE",EDGE,{"disambiguationData":[OSD([sQuery(id+"F0.wireOp",EDGE,"E12.right"),sQuery(id+"F0.wireOp",EDGE,"E16.top")])]});
            var Q3;
            Q3=makeQuery(id+"F1.opExtrude","SWEPT_EDGE",EDGE,{"disambiguationData":[OSD([sQuery(id+"F0.wireOp",EDGE,"E12.right"),sQuery(id+"F0.wireOp",EDGE,"E16.bottom")])]});
            fillet(context, id + "F21", {"entities" : qUnion([Q0, Q1, Q2, Q3]), "radius" : 10.16 * mm, "tangentPropagation" : true, "allowEdgeOverflow" : false});
        }
        {
            var Q0;
            Q0=makeQuery(id+"F1.opExtrude","CAP_EDGE",EDGE,{"disambiguationData":[OSD([sQuery(id+"F0.wireOp",EDGE,"E28.filletArc")])],"isStart":false});
            var Q1;
            Q1=makeQuery(id+"F1.opExtrude","CAP_EDGE",EDGE,{"disambiguationData":[OSD([sQuery(id+"F0.wireOp",EDGE,"E27.filletArc")])],"isStart":false});
            var Q2;
            Q2=makeQuery(id+"F6.boolean.opBoolean","INTERSECT",EDGE,{"derivedFrom":[makeQuery(id+"F1.opExtrude","CAP_FACE",FACE,{"disambiguationData":[OSD([sQuery(id+"F0.wireOp",EDGE,"E4"),sQuery(id+"F0.wireOp",EDGE,"E5"),sQuery(id+"F0.wireOp",EDGE,"E6"),sQuery(id+"F0.wireOp",EDGE,"E7"),sQuery(id+"F0.wireOp",EDGE,"E8"),sQuery(id+"F0.wireOp",EDGE,"E9"),sQuery(id+"F0.wireOp",EDGE,"E10"),sQuery(id+"F0.wireOp",EDGE,"E11"),sQuery(id+"F0.wireOp",EDGE,"E12.bottom"),sQuery(id+"F0.wireOp",EDGE,"E12.top"),sQuery(id+"F0.wireOp",EDGE,"E12.left"),sQuery(id+"F0.wireOp",EDGE,"E12.right"),sQuery(id+"F0.wireOp",EDGE,"E13.left"),sQuery(id+"F0.wireOp",EDGE,"E13.right"),sQuery(id+"F0.wireOp",EDGE,"E14.bottom"),sQuery(id+"F0.wireOp",EDGE,"E14.top"),sQuery(id+"F0.wireOp",EDGE,"E15.left"),sQuery(id+"F0.wireOp",EDGE,"E15.right"),sQuery(id+"F0.wireOp",EDGE,"E16.bottom"),sQuery(id+"F0.wireOp",EDGE,"E16.top"),sQuery(id+"F0.wireOp",EDGE,"E17.filletArc"),sQuery(id+"F0.wireOp",EDGE,"E18.filletArc"),sQuery(id+"F0.wireOp",EDGE,"E19.filletArc"),sQuery(id+"F0.wireOp",EDGE,"E20.filletArc"),sQuery(id+"F0.wireOp",EDGE,"E21.filletArc"),sQuery(id+"F0.wireOp",EDGE,"E22.filletArc"),sQuery(id+"F0.wireOp",EDGE,"E23.filletArc"),sQuery(id+"F0.wireOp",EDGE,"E24.filletArc"),sQuery(id+"F0.wireOp",EDGE,"E25.filletArc"),sQuery(id+"F0.wireOp",EDGE,"E26.filletArc"),sQuery(id+"F0.wireOp",EDGE,"E27.filletArc"),sQuery(id+"F0.wireOp",EDGE,"E28.filletArc")])],"isStart":false}),makeQuery(id+"F6.opExtrude","SWEPT_FACE",FACE,{"disambiguationData":[OSD([sQuery(id+"F5.wireOp",EDGE,"E40.left")])]})]});
            var Q3;
            Q3=makeQuery(id+"F6.boolean.opBoolean","INTERSECT",EDGE,{"derivedFrom":[makeQuery(id+"F1.opExtrude","CAP_FACE",FACE,{"disambiguationData":[OSD([sQuery(id+"F0.wireOp",EDGE,"E4"),sQuery(id+"F0.wireOp",EDGE,"E5"),sQuery(id+"F0.wireOp",EDGE,"E6"),sQuery(id+"F0.wireOp",EDGE,"E7"),sQuery(id+"F0.wireOp",EDGE,"E8"),sQuery(id+"F0.wireOp",EDGE,"E9"),sQuery(id+"F0.wireOp",EDGE,"E10"),sQuery(id+"F0.wireOp",EDGE,"E11"),sQuery(id+"F0.wireOp",EDGE,"E12.bottom"),sQuery(id+"F0.wireOp",EDGE,"E12.top"),sQuery(id+"F0.wireOp",EDGE,"E12.left"),sQuery(id+"F0.wireOp",EDGE,"E12.right"),sQuery(id+"F0.wireOp",EDGE,"E13.left"),sQuery(id+"F0.wireOp",EDGE,"E13.right"),sQuery(id+"F0.wireOp",EDGE,"E14.bottom"),sQuery(id+"F0.wireOp",EDGE,"E14.top"),sQuery(id+"F0.wireOp",EDGE,"E15.left"),sQuery(id+"F0.wireOp",EDGE,"E15.right"),sQuery(id+"F0.wireOp",EDGE,"E16.bottom"),sQuery(id+"F0.wireOp",EDGE,"E16.top"),sQuery(id+"F0.wireOp",EDGE,"E17.filletArc"),sQuery(id+"F0.wireOp",EDGE,"E18.filletArc"),sQuery(id+"F0.wireOp",EDGE,"E19.filletArc"),sQuery(id+"F0.wireOp",EDGE,"E20.filletArc"),sQuery(id+"F0.wireOp",EDGE,"E21.filletArc"),sQuery(id+"F0.wireOp",EDGE,"E22.filletArc"),sQuery(id+"F0.wireOp",EDGE,"E23.filletArc"),sQuery(id+"F0.wireOp",EDGE,"E24.filletArc"),sQuery(id+"F0.wireOp",EDGE,"E25.filletArc"),sQuery(id+"F0.wireOp",EDGE,"E26.filletArc"),sQuery(id+"F0.wireOp",EDGE,"E27.filletArc"),sQuery(id+"F0.wireOp",EDGE,"E28.filletArc")])],"isStart":false}),makeQuery(id+"F6.opExtrude","SWEPT_FACE",FACE,{"disambiguationData":[OSD([sQuery(id+"F5.wireOp",EDGE,"E41.left")])]})]});
            fillet(context, id + "F22", {"entities" : qUnion([Q0, Q1, Q2, Q3]), "radius" : 1.02 * mm, "tangentPropagation" : true, "allowEdgeOverflow" : false});
        }
        {
            var Q0;
            Q0=makeQuery(id+"F6.boolean.opBoolean","INTERSECT",EDGE,{"derivedFrom":[makeQuery(id+"F1.opExtrude","SWEPT_FACE",FACE,{"disambiguationData":[OSD([sQuery(id+"F0.wireOp",EDGE,"E28.filletArc")])]}),makeQuery(id+"F6.opExtrude","SWEPT_FACE",FACE,{"disambiguationData":[OSD([sQuery(id+"F5.wireOp",EDGE,"E37.bottom")])]})]});
            var Q1;
            Q1=makeQuery(id+"F6.boolean.opBoolean","INTERSECT",EDGE,{"derivedFrom":[makeQuery(id+"F2.opFillet","BLEND_FACE",FACE,{"disambiguationData":[OSD([sQuery(id+"F0.wireOp",EDGE,"E12.bottom"),sQuery(id+"F0.wireOp",EDGE,"E13.right")])]}),makeQuery(id+"F6.opExtrude","SWEPT_FACE",FACE,{"disambiguationData":[OSD([sQuery(id+"F5.wireOp",EDGE,"E37.bottom")])]})]});
            fillet(context, id + "F23", {"entities" : qUnion([Q0, Q1]), "radius" : 1.78 * mm, "tangentPropagation" : true, "allowEdgeOverflow" : false});
        }
        {
            var Q0;
            {var subQ0=sQuery(id+"F0.wireOp",EDGE,"E16.top");var subQ1=sQuery(id+"F0.wireOp",EDGE,"E16.bottom");var subQ2=sQuery(id+"F0.wireOp",EDGE,"E28.filletArc");var subQ3=sQuery(id+"F0.wireOp",EDGE,"E12.right");var subQ4=sQuery(id+"F0.wireOp",EDGE,"E25.filletArc");Q0=makeQuery(id+"F14.boolean.opBoolean","INTERSECT",EDGE,{"derivedFrom":[makeQuery(id+"F6.boolean.opBoolean","SPLIT",FACE,{"disambiguationData":[TD([makeQuery(id+"F1.opExtrude","SWEPT_FACE",FACE,{"disambiguationData":[OSD([subQ1])]})])],"derivedFrom":makeQuery(id+"F1.opExtrude","CAP_FACE",FACE,{"disambiguationData":[OSD([sQuery(id+"F0.wireOp",EDGE,"E4"),sQuery(id+"F0.wireOp",EDGE,"E5"),sQuery(id+"F0.wireOp",EDGE,"E6"),sQuery(id+"F0.wireOp",EDGE,"E7"),sQuery(id+"F0.wireOp",EDGE,"E8"),sQuery(id+"F0.wireOp",EDGE,"E9"),sQuery(id+"F0.wireOp",EDGE,"E10"),sQuery(id+"F0.wireOp",EDGE,"E11"),sQuery(id+"F0.wireOp",EDGE,"E12.bottom"),sQuery(id+"F0.wireOp",EDGE,"E12.top"),sQuery(id+"F0.wireOp",EDGE,"E12.left"),subQ3,sQuery(id+"F0.wireOp",EDGE,"E13.left"),sQuery(id+"F0.wireOp",EDGE,"E13.right"),sQuery(id+"F0.wireOp",EDGE,"E14.bottom"),sQuery(id+"F0.wireOp",EDGE,"E14.top"),sQuery(id+"F0.wireOp",EDGE,"E15.left"),sQuery(id+"F0.wireOp",EDGE,"E15.right"),subQ1,subQ0,sQuery(id+"F0.wireOp",EDGE,"E17.filletArc"),sQuery(id+"F0.wireOp",EDGE,"E18.filletArc"),sQuery(id+"F0.wireOp",EDGE,"E19.filletArc"),sQuery(id+"F0.wireOp",EDGE,"E20.filletArc"),sQuery(id+"F0.wireOp",EDGE,"E21.filletArc"),sQuery(id+"F0.wireOp",EDGE,"E22.filletArc"),sQuery(id+"F0.wireOp",EDGE,"E23.filletArc"),sQuery(id+"F0.wireOp",EDGE,"E24.filletArc"),subQ4,sQuery(id+"F0.wireOp",EDGE,"E26.filletArc"),sQuery(id+"F0.wireOp",EDGE,"E27.filletArc"),subQ2])],"isStart":false})}),makeQuery(id+"F14.opExtrude","SWEPT_FACE",FACE,{"disambiguationData":[OSD([sQuery(id+"F13.wireOp",EDGE,"E47.top")])]})]});}
            var Q1;
            {var subQ0=sQuery(id+"F0.wireOp",EDGE,"E16.top");var subQ1=sQuery(id+"F0.wireOp",EDGE,"E16.bottom");var subQ2=sQuery(id+"F0.wireOp",EDGE,"E28.filletArc");var subQ3=sQuery(id+"F0.wireOp",EDGE,"E12.right");var subQ4=sQuery(id+"F0.wireOp",EDGE,"E25.filletArc");Q1=makeQuery(id+"F14.boolean.opBoolean","INTERSECT",EDGE,{"derivedFrom":[makeQuery(id+"F6.boolean.opBoolean","SPLIT",FACE,{"disambiguationData":[TD([makeQuery(id+"F1.opExtrude","SWEPT_FACE",FACE,{"disambiguationData":[OSD([subQ1])]})])],"derivedFrom":makeQuery(id+"F1.opExtrude","CAP_FACE",FACE,{"disambiguationData":[OSD([sQuery(id+"F0.wireOp",EDGE,"E4"),sQuery(id+"F0.wireOp",EDGE,"E5"),sQuery(id+"F0.wireOp",EDGE,"E6"),sQuery(id+"F0.wireOp",EDGE,"E7"),sQuery(id+"F0.wireOp",EDGE,"E8"),sQuery(id+"F0.wireOp",EDGE,"E9"),sQuery(id+"F0.wireOp",EDGE,"E10"),sQuery(id+"F0.wireOp",EDGE,"E11"),sQuery(id+"F0.wireOp",EDGE,"E12.bottom"),sQuery(id+"F0.wireOp",EDGE,"E12.top"),sQuery(id+"F0.wireOp",EDGE,"E12.left"),subQ3,sQuery(id+"F0.wireOp",EDGE,"E13.left"),sQuery(id+"F0.wireOp",EDGE,"E13.right"),sQuery(id+"F0.wireOp",EDGE,"E14.bottom"),sQuery(id+"F0.wireOp",EDGE,"E14.top"),sQuery(id+"F0.wireOp",EDGE,"E15.left"),sQuery(id+"F0.wireOp",EDGE,"E15.right"),subQ1,subQ0,sQuery(id+"F0.wireOp",EDGE,"E17.filletArc"),sQuery(id+"F0.wireOp",EDGE,"E18.filletArc"),sQuery(id+"F0.wireOp",EDGE,"E19.filletArc"),sQuery(id+"F0.wireOp",EDGE,"E20.filletArc"),sQuery(id+"F0.wireOp",EDGE,"E21.filletArc"),sQuery(id+"F0.wireOp",EDGE,"E22.filletArc"),sQuery(id+"F0.wireOp",EDGE,"E23.filletArc"),sQuery(id+"F0.wireOp",EDGE,"E24.filletArc"),subQ4,sQuery(id+"F0.wireOp",EDGE,"E26.filletArc"),sQuery(id+"F0.wireOp",EDGE,"E27.filletArc"),subQ2])],"isStart":false})}),makeQuery(id+"F14.opExtrude","SWEPT_FACE",FACE,{"disambiguationData":[OSD([sQuery(id+"F13.wireOp",EDGE,"E47.bottom")])]})]});}
            var Q2;
            {var subQ0=sQuery(id+"F3.wireOp",EDGE,"E33");Q2=makeQuery(id+"F14.boolean.opBoolean","SPLIT",EDGE,{"disambiguationData":[TD([makeQuery(id+"F14.opExtrude","SWEPT_FACE",FACE,{"disambiguationData":[OSD([sQuery(id+"F13.wireOp",EDGE,"E47.right")])]})])],"derivedFrom":makeQuery(id+"F4.boolean.opBoolean","COPY",EDGE,{"derivedFrom":makeQuery(id+"F4.opExtrude","CAP_EDGE",EDGE,{"disambiguationData":[OSD([subQ0])],"isStart":true})})});}
            var Q3;
            {var subQ0=sQuery(id+"F0.wireOp",EDGE,"E14.top");var subQ1=sQuery(id+"F0.wireOp",EDGE,"E14.bottom");var subQ2=sQuery(id+"F0.wireOp",EDGE,"E27.filletArc");var subQ3=sQuery(id+"F0.wireOp",EDGE,"E12.left");var subQ4=sQuery(id+"F0.wireOp",EDGE,"E26.filletArc");Q3=makeQuery(id+"F17.boolean.opBoolean","INTERSECT",EDGE,{"derivedFrom":[makeQuery(id+"F6.boolean.opBoolean","SPLIT",FACE,{"disambiguationData":[TD([makeQuery(id+"F1.opExtrude","SWEPT_FACE",FACE,{"disambiguationData":[OSD([subQ1])]})])],"derivedFrom":makeQuery(id+"F1.opExtrude","CAP_FACE",FACE,{"disambiguationData":[OSD([sQuery(id+"F0.wireOp",EDGE,"E4"),sQuery(id+"F0.wireOp",EDGE,"E5"),sQuery(id+"F0.wireOp",EDGE,"E6"),sQuery(id+"F0.wireOp",EDGE,"E7"),sQuery(id+"F0.wireOp",EDGE,"E8"),sQuery(id+"F0.wireOp",EDGE,"E9"),sQuery(id+"F0.wireOp",EDGE,"E10"),sQuery(id+"F0.wireOp",EDGE,"E11"),sQuery(id+"F0.wireOp",EDGE,"E12.bottom"),sQuery(id+"F0.wireOp",EDGE,"E12.top"),subQ3,sQuery(id+"F0.wireOp",EDGE,"E12.right"),sQuery(id+"F0.wireOp",EDGE,"E13.left"),sQuery(id+"F0.wireOp",EDGE,"E13.right"),subQ1,subQ0,sQuery(id+"F0.wireOp",EDGE,"E15.left"),sQuery(id+"F0.wireOp",EDGE,"E15.right"),sQuery(id+"F0.wireOp",EDGE,"E16.bottom"),sQuery(id+"F0.wireOp",EDGE,"E16.top"),sQuery(id+"F0.wireOp",EDGE,"E17.filletArc"),sQuery(id+"F0.wireOp",EDGE,"E18.filletArc"),sQuery(id+"F0.wireOp",EDGE,"E19.filletArc"),sQuery(id+"F0.wireOp",EDGE,"E20.filletArc"),sQuery(id+"F0.wireOp",EDGE,"E21.filletArc"),sQuery(id+"F0.wireOp",EDGE,"E22.filletArc"),sQuery(id+"F0.wireOp",EDGE,"E23.filletArc"),sQuery(id+"F0.wireOp",EDGE,"E24.filletArc"),sQuery(id+"F0.wireOp",EDGE,"E25.filletArc"),subQ4,subQ2,sQuery(id+"F0.wireOp",EDGE,"E28.filletArc")])],"isStart":false})}),makeQuery(id+"F17.opExtrude","SWEPT_FACE",FACE,{"disambiguationData":[OSD([sQuery(id+"F16.wireOp",EDGE,"E48.bottom")])]})]});}
            var Q4;
            {var subQ0=sQuery(id+"F0.wireOp",EDGE,"E14.top");var subQ1=sQuery(id+"F0.wireOp",EDGE,"E14.bottom");var subQ2=sQuery(id+"F0.wireOp",EDGE,"E27.filletArc");var subQ3=sQuery(id+"F0.wireOp",EDGE,"E12.left");var subQ4=sQuery(id+"F0.wireOp",EDGE,"E26.filletArc");Q4=makeQuery(id+"F17.boolean.opBoolean","INTERSECT",EDGE,{"disambiguationData":[OD(1.0)],"derivedFrom":[makeQuery(id+"F6.boolean.opBoolean","SPLIT",FACE,{"disambiguationData":[TD([makeQuery(id+"F1.opExtrude","SWEPT_FACE",FACE,{"disambiguationData":[OSD([subQ1])]})])],"derivedFrom":makeQuery(id+"F1.opExtrude","CAP_FACE",FACE,{"disambiguationData":[OSD([sQuery(id+"F0.wireOp",EDGE,"E4"),sQuery(id+"F0.wireOp",EDGE,"E5"),sQuery(id+"F0.wireOp",EDGE,"E6"),sQuery(id+"F0.wireOp",EDGE,"E7"),sQuery(id+"F0.wireOp",EDGE,"E8"),sQuery(id+"F0.wireOp",EDGE,"E9"),sQuery(id+"F0.wireOp",EDGE,"E10"),sQuery(id+"F0.wireOp",EDGE,"E11"),sQuery(id+"F0.wireOp",EDGE,"E12.bottom"),sQuery(id+"F0.wireOp",EDGE,"E12.top"),subQ3,sQuery(id+"F0.wireOp",EDGE,"E12.right"),sQuery(id+"F0.wireOp",EDGE,"E13.left"),sQuery(id+"F0.wireOp",EDGE,"E13.right"),subQ1,subQ0,sQuery(id+"F0.wireOp",EDGE,"E15.left"),sQuery(id+"F0.wireOp",EDGE,"E15.right"),sQuery(id+"F0.wireOp",EDGE,"E16.bottom"),sQuery(id+"F0.wireOp",EDGE,"E16.top"),sQuery(id+"F0.wireOp",EDGE,"E17.filletArc"),sQuery(id+"F0.wireOp",EDGE,"E18.filletArc"),sQuery(id+"F0.wireOp",EDGE,"E19.filletArc"),sQuery(id+"F0.wireOp",EDGE,"E20.filletArc"),sQuery(id+"F0.wireOp",EDGE,"E21.filletArc"),sQuery(id+"F0.wireOp",EDGE,"E22.filletArc"),sQuery(id+"F0.wireOp",EDGE,"E23.filletArc"),sQuery(id+"F0.wireOp",EDGE,"E24.filletArc"),sQuery(id+"F0.wireOp",EDGE,"E25.filletArc"),subQ4,subQ2,sQuery(id+"F0.wireOp",EDGE,"E28.filletArc")])],"isStart":false})}),makeQuery(id+"F17.opExtrude","SWEPT_FACE",FACE,{"disambiguationData":[OSD([sQuery(id+"F16.wireOp",EDGE,"E48.right")])]})]});}
            fillet(context, id + "F24", {"entities" : qUnion([Q0, Q1, Q2, Q3, Q4]), "radius" : 0.38 * mm, "tangentPropagation" : true, "allowEdgeOverflow" : false});
        }
        {
            var Q0;
            Q0=makeQuery(id+"F6.boolean.opBoolean","INTERSECT",EDGE,{"derivedFrom":[makeQuery(id+"F4.boolean.opBoolean","COPY",FACE,{"derivedFrom":makeQuery(id+"F4.opExtrude","SWEPT_FACE",FACE,{"disambiguationData":[OSD([sQuery(id+"F3.wireOp",EDGE,"E36")])]})}),makeQuery(id+"F6.opExtrude","SWEPT_FACE",FACE,{"disambiguationData":[OSD([sQuery(id+"F5.wireOp",EDGE,"E42.filletArc")])]})]});
            var Q1;
            Q1=makeQuery(id+"F6.boolean.opBoolean","INTERSECT",EDGE,{"derivedFrom":[makeQuery(id+"F4.boolean.opBoolean","COPY",FACE,{"derivedFrom":makeQuery(id+"F4.opExtrude","SWEPT_FACE",FACE,{"disambiguationData":[OSD([sQuery(id+"F3.wireOp",EDGE,"E36")])]})}),makeQuery(id+"F6.opExtrude","SWEPT_FACE",FACE,{"disambiguationData":[OSD([sQuery(id+"F5.wireOp",EDGE,"E41.bottom")])]})]});
            var Q2;
            Q2=makeQuery(id+"F4.boolean.opBoolean","INTERSECT",EDGE,{"derivedFrom":[makeQuery(id+"F1.opExtrude","SWEPT_FACE",FACE,{"disambiguationData":[OSD([sQuery(id+"F0.wireOp",EDGE,"E11")])]}),makeQuery(id+"F4.opExtrude","CAP_FACE",FACE,{"disambiguationData":[OSD([sQuery(id+"F3.wireOp",EDGE,"E36")])],"isStart":false})]});
            var Q3;
            Q3=makeQuery(id+"F4.boolean.opBoolean","INTERSECT",EDGE,{"derivedFrom":[makeQuery(id+"F1.opExtrude","SWEPT_FACE",FACE,{"disambiguationData":[OSD([sQuery(id+"F0.wireOp",EDGE,"E5")])]}),makeQuery(id+"F4.opExtrude","CAP_FACE",FACE,{"disambiguationData":[OSD([sQuery(id+"F3.wireOp",EDGE,"E33")])],"isStart":false})]});
            var Q4;
            Q4=makeQuery(id+"F14.boolean.opBoolean","INTERSECT",EDGE,{"disambiguationData":[OD(1.0)],"derivedFrom":[makeQuery(id+"F4.boolean.opBoolean","COPY",FACE,{"derivedFrom":makeQuery(id+"F4.opExtrude","SWEPT_FACE",FACE,{"disambiguationData":[OSD([sQuery(id+"F3.wireOp",EDGE,"E33")])]})}),makeQuery(id+"F14.opExtrude","SWEPT_FACE",FACE,{"disambiguationData":[OSD([sQuery(id+"F13.wireOp",EDGE,"E47.right")])]})]});
            var Q5;
            Q5=makeQuery(id+"F14.boolean.opBoolean","INTERSECT",EDGE,{"disambiguationData":[OD(0.0)],"derivedFrom":[makeQuery(id+"F4.boolean.opBoolean","COPY",FACE,{"derivedFrom":makeQuery(id+"F4.opExtrude","SWEPT_FACE",FACE,{"disambiguationData":[OSD([sQuery(id+"F3.wireOp",EDGE,"E33")])]})}),makeQuery(id+"F14.opExtrude","SWEPT_FACE",FACE,{"disambiguationData":[OSD([sQuery(id+"F13.wireOp",EDGE,"E47.right")])]})]});
            var Q6;
            Q6=makeQuery(id+"F4.boolean.opBoolean","COPY",EDGE,{"derivedFrom":makeQuery(id+"F4.opExtrude","CAP_EDGE",EDGE,{"disambiguationData":[OSD([sQuery(id+"F3.wireOp",EDGE,"E36")])],"isStart":false})});
            var Q7;
            Q7=makeQuery(id+"F4.boolean.opBoolean","COPY",EDGE,{"derivedFrom":makeQuery(id+"F4.opExtrude","CAP_EDGE",EDGE,{"disambiguationData":[OSD([sQuery(id+"F3.wireOp",EDGE,"E33")])],"isStart":false})});
            var Q8;
            Q8=makeQuery(id+"F4.boolean.opBoolean","COPY",EDGE,{"derivedFrom":makeQuery(id+"F4.opExtrude","CAP_EDGE",EDGE,{"disambiguationData":[OSD([sQuery(id+"F3.wireOp",EDGE,"E34")])],"isStart":false})});
            var Q9;
            {var subQ0=sQuery(id+"F3.wireOp",EDGE,"E34");Q9=makeQuery(id+"F17.boolean.opBoolean","SPLIT",EDGE,{"disambiguationData":[TD([makeQuery(id+"F17.opExtrude","SWEPT_FACE",FACE,{"disambiguationData":[OSD([sQuery(id+"F16.wireOp",EDGE,"E48.right")])]})])],"derivedFrom":makeQuery(id+"F4.boolean.opBoolean","COPY",EDGE,{"derivedFrom":makeQuery(id+"F4.opExtrude","CAP_EDGE",EDGE,{"disambiguationData":[OSD([subQ0])],"isStart":true})})});}
            var Q10;
            Q10=makeQuery(id+"F17.boolean.opBoolean","INTERSECT",EDGE,{"disambiguationData":[OD(0.0)],"derivedFrom":[makeQuery(id+"F4.boolean.opBoolean","COPY",FACE,{"derivedFrom":makeQuery(id+"F4.opExtrude","SWEPT_FACE",FACE,{"disambiguationData":[OSD([sQuery(id+"F3.wireOp",EDGE,"E34")])]})}),makeQuery(id+"F17.opExtrude","SWEPT_FACE",FACE,{"disambiguationData":[OSD([sQuery(id+"F16.wireOp",EDGE,"E48.right")])]})]});
            var Q11;
            Q11=makeQuery(id+"F6.boolean.opBoolean","INTERSECT",EDGE,{"derivedFrom":[makeQuery(id+"F4.boolean.opBoolean","COPY",FACE,{"derivedFrom":makeQuery(id+"F4.opExtrude","SWEPT_FACE",FACE,{"disambiguationData":[OSD([sQuery(id+"F3.wireOp",EDGE,"E35")])]})}),makeQuery(id+"F6.opExtrude","SWEPT_FACE",FACE,{"disambiguationData":[OSD([sQuery(id+"F5.wireOp",EDGE,"E43.filletArc")])]})]});
            var Q12;
            Q12=makeQuery(id+"F6.boolean.opBoolean","INTERSECT",EDGE,{"derivedFrom":[makeQuery(id+"F4.boolean.opBoolean","COPY",FACE,{"derivedFrom":makeQuery(id+"F4.opExtrude","SWEPT_FACE",FACE,{"disambiguationData":[OSD([sQuery(id+"F3.wireOp",EDGE,"E35")])]})}),makeQuery(id+"F6.opExtrude","SWEPT_FACE",FACE,{"disambiguationData":[OSD([sQuery(id+"F5.wireOp",EDGE,"E40.bottom")])]})]});
            var Q13;
            Q13=makeQuery(id+"F4.boolean.opBoolean","COPY",EDGE,{"derivedFrom":makeQuery(id+"F4.opExtrude","CAP_EDGE",EDGE,{"disambiguationData":[OSD([sQuery(id+"F3.wireOp",EDGE,"E35")])],"isStart":false})});
            var Q14;
            Q14=makeQuery(id+"F4.boolean.opBoolean","INTERSECT",EDGE,{"derivedFrom":[makeQuery(id+"F1.opExtrude","SWEPT_FACE",FACE,{"disambiguationData":[OSD([sQuery(id+"F0.wireOp",EDGE,"E10")])]}),makeQuery(id+"F4.opExtrude","CAP_FACE",FACE,{"disambiguationData":[OSD([sQuery(id+"F3.wireOp",EDGE,"E35")])],"isStart":false})]});
            var Q15;
            Q15=makeQuery(id+"F4.boolean.opBoolean","INTERSECT",EDGE,{"derivedFrom":[makeQuery(id+"F1.opExtrude","SWEPT_FACE",FACE,{"disambiguationData":[OSD([sQuery(id+"F0.wireOp",EDGE,"E7")])]}),makeQuery(id+"F4.opExtrude","CAP_FACE",FACE,{"disambiguationData":[OSD([sQuery(id+"F3.wireOp",EDGE,"E34")])],"isStart":false})]});
            fillet(context, id + "F25", {"entities" : qUnion([Q0, Q1, Q2, Q3, Q4, Q5, Q6, Q7, Q8, Q9, Q10, Q11, Q12, Q13, Q14, Q15]), "radius" : 0.25 * mm, "allowEdgeOverflow" : false});
        }
        {
            var Q0;
            Q0=makeQuery(id+"F6.boolean.opBoolean","INTERSECT",EDGE,{"derivedFrom":[makeQuery(id+"F4.boolean.opBoolean","COPY",FACE,{"derivedFrom":makeQuery(id+"F4.opExtrude","SWEPT_FACE",FACE,{"disambiguationData":[OSD([sQuery(id+"F3.wireOp",EDGE,"E30")])]})}),makeQuery(id+"F6.opExtrude","SWEPT_FACE",FACE,{"disambiguationData":[OSD([sQuery(id+"F5.wireOp",EDGE,"E37.bottom")])]})]});
            var Q1;
            Q1=makeQuery(id+"F4.boolean.opBoolean","INTERSECT",EDGE,{"derivedFrom":[makeQuery(id+"F1.opExtrude","SWEPT_FACE",FACE,{"disambiguationData":[OSD([sQuery(id+"F0.wireOp",EDGE,"E4")])]}),makeQuery(id+"F4.opExtrude","CAP_FACE",FACE,{"disambiguationData":[OSD([sQuery(id+"F3.wireOp",EDGE,"E30")])],"isStart":false})]});
            var Q2;
            Q2=makeQuery(id+"F6.boolean.opBoolean","INTERSECT",EDGE,{"derivedFrom":[makeQuery(id+"F4.boolean.opBoolean","COPY",FACE,{"derivedFrom":makeQuery(id+"F4.opExtrude","SWEPT_FACE",FACE,{"disambiguationData":[OSD([sQuery(id+"F3.wireOp",EDGE,"E29")])]})}),makeQuery(id+"F6.opExtrude","SWEPT_FACE",FACE,{"disambiguationData":[OSD([sQuery(id+"F5.wireOp",EDGE,"E37.bottom")])]})]});
            var Q3;
            Q3=makeQuery(id+"F4.boolean.opBoolean","INTERSECT",EDGE,{"derivedFrom":[makeQuery(id+"F1.opExtrude","SWEPT_FACE",FACE,{"disambiguationData":[OSD([sQuery(id+"F0.wireOp",EDGE,"E8")])]}),makeQuery(id+"F4.opExtrude","CAP_FACE",FACE,{"disambiguationData":[OSD([sQuery(id+"F3.wireOp",EDGE,"E29")])],"isStart":false})]});
            var Q4;
            Q4=makeQuery(id+"F6.boolean.opBoolean","INTERSECT",EDGE,{"derivedFrom":[makeQuery(id+"F4.boolean.opBoolean","COPY",FACE,{"derivedFrom":makeQuery(id+"F4.opExtrude","SWEPT_FACE",FACE,{"disambiguationData":[OSD([sQuery(id+"F3.wireOp",EDGE,"E31")])]})}),makeQuery(id+"F6.opExtrude","SWEPT_FACE",FACE,{"disambiguationData":[OSD([sQuery(id+"F5.wireOp",EDGE,"E37.bottom")])]})]});
            var Q5;
            Q5=makeQuery(id+"F4.boolean.opBoolean","INTERSECT",EDGE,{"derivedFrom":[makeQuery(id+"F1.opExtrude","SWEPT_FACE",FACE,{"disambiguationData":[OSD([sQuery(id+"F0.wireOp",EDGE,"E6")])]}),makeQuery(id+"F4.opExtrude","CAP_FACE",FACE,{"disambiguationData":[OSD([sQuery(id+"F3.wireOp",EDGE,"E31")])],"isStart":false})]});
            var Q6;
            Q6=makeQuery(id+"F6.boolean.opBoolean","INTERSECT",EDGE,{"derivedFrom":[makeQuery(id+"F4.boolean.opBoolean","COPY",FACE,{"derivedFrom":makeQuery(id+"F4.opExtrude","SWEPT_FACE",FACE,{"disambiguationData":[OSD([sQuery(id+"F3.wireOp",EDGE,"E32")])]})}),makeQuery(id+"F6.opExtrude","SWEPT_FACE",FACE,{"disambiguationData":[OSD([sQuery(id+"F5.wireOp",EDGE,"E37.bottom")])]})]});
            var Q7;
            Q7=makeQuery(id+"F23.opFillet","BLEND_EDGE",EDGE,{"disambiguationData":[OD(0.0)],"blendedFrom":[makeQuery(id+"F6.boolean.opBoolean","INTERSECT",EDGE,{"derivedFrom":[makeQuery(id+"F2.opFillet","BLEND_FACE",FACE,{"disambiguationData":[OSD([sQuery(id+"F0.wireOp",EDGE,"E12.top"),sQuery(id+"F0.wireOp",EDGE,"E15.left")])]}),makeQuery(id+"F6.opExtrude","SWEPT_FACE",FACE,{"disambiguationData":[OSD([sQuery(id+"F5.wireOp",EDGE,"E37.bottom")])]})]}),makeQuery(id+"F4.boolean.opBoolean","COPY",FACE,{"derivedFrom":makeQuery(id+"F4.opExtrude","SWEPT_FACE",FACE,{"disambiguationData":[OSD([sQuery(id+"F3.wireOp",EDGE,"E32")])]})})],"blendedInto":[makeQuery(id+"F4.boolean.opBoolean","COPY",FACE,{"derivedFrom":makeQuery(id+"F4.opExtrude","SWEPT_FACE",FACE,{"disambiguationData":[OSD([sQuery(id+"F3.wireOp",EDGE,"E32")])]})})]});
            var Q8;
            Q8=makeQuery(id+"F4.boolean.opBoolean","INTERSECT",EDGE,{"derivedFrom":[makeQuery(id+"F1.opExtrude","SWEPT_FACE",FACE,{"disambiguationData":[OSD([sQuery(id+"F0.wireOp",EDGE,"E9")])]}),makeQuery(id+"F4.opExtrude","CAP_FACE",FACE,{"disambiguationData":[OSD([sQuery(id+"F3.wireOp",EDGE,"E32")])],"isStart":false})]});
            var Q9;
            Q9=makeQuery(id+"F4.boolean.opBoolean","COPY",EDGE,{"derivedFrom":makeQuery(id+"F4.opExtrude","CAP_EDGE",EDGE,{"disambiguationData":[OSD([sQuery(id+"F3.wireOp",EDGE,"E32")])],"isStart":false})});
            var Q10;
            Q10=makeQuery(id+"F4.boolean.opBoolean","COPY",EDGE,{"derivedFrom":makeQuery(id+"F4.opExtrude","CAP_EDGE",EDGE,{"disambiguationData":[OSD([sQuery(id+"F3.wireOp",EDGE,"E31")])],"isStart":false})});
            var Q11;
            Q11=makeQuery(id+"F4.boolean.opBoolean","COPY",EDGE,{"derivedFrom":makeQuery(id+"F4.opExtrude","CAP_EDGE",EDGE,{"disambiguationData":[OSD([sQuery(id+"F3.wireOp",EDGE,"E29")])],"isStart":false})});
            var Q12;
            Q12=makeQuery(id+"F4.boolean.opBoolean","COPY",EDGE,{"derivedFrom":makeQuery(id+"F4.opExtrude","CAP_EDGE",EDGE,{"disambiguationData":[OSD([sQuery(id+"F3.wireOp",EDGE,"E30")])],"isStart":false})});
            fillet(context, id + "F26", {"entities" : qUnion([Q0, Q1, Q2, Q3, Q4, Q5, Q6, Q7, Q8, Q9, Q10, Q11, Q12]), "radius" : 0.25 * mm, "tangentPropagation" : true, "allowEdgeOverflow" : false});
        }
        {
            var Q0;
            Q0=makeQuery(id+"F1.opExtrude","CAP_EDGE",EDGE,{"disambiguationData":[OSD([sQuery(id+"F0.wireOp",EDGE,"E9")])],"isStart":true});
            var Q1;
            Q1=makeQuery(id+"F1.opExtrude","CAP_EDGE",EDGE,{"disambiguationData":[OSD([sQuery(id+"F0.wireOp",EDGE,"E6")])],"isStart":true});
            var Q2;
            Q2=makeQuery(id+"F1.opExtrude","CAP_EDGE",EDGE,{"disambiguationData":[OSD([sQuery(id+"F0.wireOp",EDGE,"E4")])],"isStart":true});
            var Q3;
            Q3=makeQuery(id+"F1.opExtrude","CAP_EDGE",EDGE,{"disambiguationData":[OSD([sQuery(id+"F0.wireOp",EDGE,"E8")])],"isStart":true});
            var Q4;
            Q4=makeQuery(id+"F1.opExtrude","CAP_EDGE",EDGE,{"disambiguationData":[OSD([sQuery(id+"F0.wireOp",EDGE,"E7")])],"isStart":true});
            var Q5;
            Q5=makeQuery(id+"F1.opExtrude","CAP_EDGE",EDGE,{"disambiguationData":[OSD([sQuery(id+"F0.wireOp",EDGE,"E10")])],"isStart":true});
            var Q6;
            Q6=makeQuery(id+"F1.opExtrude","CAP_EDGE",EDGE,{"disambiguationData":[OSD([sQuery(id+"F0.wireOp",EDGE,"E5")])],"isStart":true});
            var Q7;
            Q7=makeQuery(id+"F1.opExtrude","CAP_EDGE",EDGE,{"disambiguationData":[OSD([sQuery(id+"F0.wireOp",EDGE,"E11")])],"isStart":true});
            var Q8;
            Q8=makeQuery(id+"F1.opExtrude","CAP_EDGE",EDGE,{"disambiguationData":[OSD([sQuery(id+"F0.wireOp",EDGE,"E25.filletArc")])],"isStart":true});
            var Q9;
            Q9=makeQuery(id+"F17.boolean.opBoolean","INTERSECT",EDGE,{"derivedFrom":[makeQuery(id+"F1.opExtrude","CAP_FACE",FACE,{"disambiguationData":[OSD([sQuery(id+"F0.wireOp",EDGE,"E4"),sQuery(id+"F0.wireOp",EDGE,"E5"),sQuery(id+"F0.wireOp",EDGE,"E6"),sQuery(id+"F0.wireOp",EDGE,"E7"),sQuery(id+"F0.wireOp",EDGE,"E8"),sQuery(id+"F0.wireOp",EDGE,"E9"),sQuery(id+"F0.wireOp",EDGE,"E10"),sQuery(id+"F0.wireOp",EDGE,"E11"),sQuery(id+"F0.wireOp",EDGE,"E12.bottom"),sQuery(id+"F0.wireOp",EDGE,"E12.top"),sQuery(id+"F0.wireOp",EDGE,"E12.left"),sQuery(id+"F0.wireOp",EDGE,"E12.right"),sQuery(id+"F0.wireOp",EDGE,"E13.left"),sQuery(id+"F0.wireOp",EDGE,"E13.right"),sQuery(id+"F0.wireOp",EDGE,"E14.bottom"),sQuery(id+"F0.wireOp",EDGE,"E14.top"),sQuery(id+"F0.wireOp",EDGE,"E15.left"),sQuery(id+"F0.wireOp",EDGE,"E15.right"),sQuery(id+"F0.wireOp",EDGE,"E16.bottom"),sQuery(id+"F0.wireOp",EDGE,"E16.top"),sQuery(id+"F0.wireOp",EDGE,"E17.filletArc"),sQuery(id+"F0.wireOp",EDGE,"E18.filletArc"),sQuery(id+"F0.wireOp",EDGE,"E19.filletArc"),sQuery(id+"F0.wireOp",EDGE,"E20.filletArc"),sQuery(id+"F0.wireOp",EDGE,"E21.filletArc"),sQuery(id+"F0.wireOp",EDGE,"E22.filletArc"),sQuery(id+"F0.wireOp",EDGE,"E23.filletArc"),sQuery(id+"F0.wireOp",EDGE,"E24.filletArc"),sQuery(id+"F0.wireOp",EDGE,"E25.filletArc"),sQuery(id+"F0.wireOp",EDGE,"E26.filletArc"),sQuery(id+"F0.wireOp",EDGE,"E27.filletArc"),sQuery(id+"F0.wireOp",EDGE,"E28.filletArc")])],"isStart":true}),makeQuery(id+"F17.opExtrude","SWEPT_FACE",FACE,{"disambiguationData":[OSD([sQuery(id+"F16.wireOp",EDGE,"E48.bottom")])]})]});
            fillet(context, id + "F27", {"entities" : qUnion([Q0, Q1, Q2, Q3, Q4, Q5, Q6, Q7, Q8, Q9]), "radius" : 0.25 * mm, "tangentPropagation" : true, "allowEdgeOverflow" : false});
        }
        {
            var Q0;
            Q0=makeQuery(id+"F21.opFillet","BLEND_EDGE",EDGE,{"blendedFrom":[makeQuery(id+"F1.opExtrude","SWEPT_EDGE",EDGE,{"disambiguationData":[OSD([sQuery(id+"F0.wireOp",EDGE,"E12.right"),sQuery(id+"F0.wireOp",EDGE,"E16.top")])]}),makeQuery(id+"F6.boolean.opBoolean","COPY",FACE,{"derivedFrom":makeQuery(id+"F6.opExtrude","SWEPT_FACE",FACE,{"disambiguationData":[OSD([sQuery(id+"F5.wireOp",EDGE,"E42.filletArc")])]})})],"blendedInto":[makeQuery(id+"F6.boolean.opBoolean","COPY",FACE,{"derivedFrom":makeQuery(id+"F6.opExtrude","SWEPT_FACE",FACE,{"disambiguationData":[OSD([sQuery(id+"F5.wireOp",EDGE,"E42.filletArc")])]})})]});
            var Q1;
            Q1=makeQuery(id+"F21.opFillet","BLEND_EDGE",EDGE,{"blendedFrom":[makeQuery(id+"F1.opExtrude","SWEPT_EDGE",EDGE,{"disambiguationData":[OSD([sQuery(id+"F0.wireOp",EDGE,"E12.left"),sQuery(id+"F0.wireOp",EDGE,"E14.top")])]}),makeQuery(id+"F6.boolean.opBoolean","COPY",FACE,{"derivedFrom":makeQuery(id+"F6.opExtrude","SWEPT_FACE",FACE,{"disambiguationData":[OSD([sQuery(id+"F5.wireOp",EDGE,"E43.filletArc")])]})})],"blendedInto":[makeQuery(id+"F6.boolean.opBoolean","COPY",FACE,{"derivedFrom":makeQuery(id+"F6.opExtrude","SWEPT_FACE",FACE,{"disambiguationData":[OSD([sQuery(id+"F5.wireOp",EDGE,"E43.filletArc")])]})})]});
            fillet(context, id + "F28", {"entities" : qUnion([Q0, Q1]), "radius" : 0.5 * mm, "tangentPropagation" : true, "allowEdgeOverflow" : false});
        }
    });
